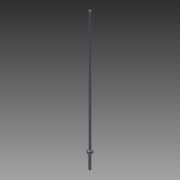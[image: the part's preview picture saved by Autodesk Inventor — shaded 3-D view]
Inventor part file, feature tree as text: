
AUTODESK INVENTOR PART (.ipt)
format: ipt  version: 2011 (Build 150239000, 239)  size: 293,888 bytes
history: native  units: mm (DEFAULTED — no unit token found)
features: other x8, plane x3, sketch x3, extrude x2, pattern_circular x1
ambient origin geometry x5: Origin, X Axis, Y Axis, Z Axis, Center Point
bodies: Solid1 (feature_tree)
feature tree (17):
  other  "Tooth Plane"
  other  "Base Body Sketch"
  other  "Base Body"
  other  "Base Body2"
  plane  "Work Plane13"
  other  "Tooth"
  pattern_circular  "Tooth Pattern"  [2 undecoded]
  plane  "Work Plane14"
  plane  "Work Plane15"
  extrude  "Extrusion1"  Depth=1.275119mm
  extrude  "Extrusion3"  Depth=1.677788mm
  other  "Tooth Sketch"
  sketch  "Sketch8"  dims[d35=90.0deg]
  other  "Srf1"
  sketch  "Sketch9"  dims[d37=-0.996687mm]
  sketch  "Sketch11"  dims[d38=3.355575mm d39=3.490659mm d40=1.275119mm d41=1.677788mm d42=0.316256mm d43=90.0deg d44=100.0mm d46=360.0deg d50=7.019286mm d68=3.355575mm d69=0.0mm d73=0.0mm d75=3.141593mm d77=3.355575mm d78=2.6mm d79=0.0mm d80=0.0mm d81=0.0mm d82=0.0mm d83=3.141593mm d84=0.0mm d85=180.0deg d86=3.355575mm d87=4.362248mm d89=2.68446mm d90=90.0deg d92=2.6mm d93=3.355575mm d94=2.0mm d95=113.224mm d96=0.0mm d99=2.0mm d100=13.276mm d101=0.0mm]
  other  "Pitch Diameter"
note: 2 required parameter values undecoded (feature->parameter linkage not recoverable at this tier; creation-order binding heuristic only, values carry confidence <= 0.55)
